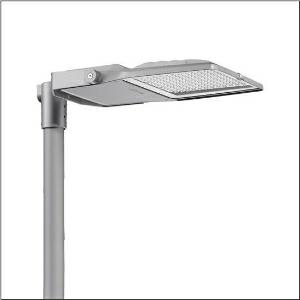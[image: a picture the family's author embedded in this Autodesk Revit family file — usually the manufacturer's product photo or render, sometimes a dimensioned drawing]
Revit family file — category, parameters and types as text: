
# Revit family: floodlight_fl_21_iq_midi___pl33t_5xa7781f4f3a_8e83
name_source: partatom
category: Lighting Fixtures
units: mm (PartAtom-declared; Revit-internal decimal feet)

## family parameters
Cut with Voids When Loaded = No
Host = Face
Light Source = No
Part Type = Normal
Room Calculation Point = No
Round Connector Dimension = Use Diameter
Shared = No

## types (1)
- --- (1 x LED, 36900 lm, 270.2 W, 4000K)
    Apparent Load = 270 VA
    CIE Flux Codes = 26 75 99 100 100
    Color Rendering = 70
    Color Temperature = 4000K
    Default Elevation = 1800 mm
    Description = Floodlight FL 21 iQ midi, floodlight, primary light control with lens, of PMMA, primary optical cover: protective disc, of toughened safety glass, transparent, light distribution: PL33T, light emission: direct distribution, installation type: surface-mounted, LED, High Power LED, rated luminous flux: 36.900lm, luminous efficacy: 137lm/W, light colour: 740, colour temperature: 4000K, control gear: iQ Comfort/DALI, control: optimised constant luminous flux control (CLO 2.0), Desk-Remote (wireless, voltage-free reading and setting of iQ features in the workshop via application-optimized NFC function/RFID function), Light-Fading, Smart-Wire, Night-Set, Lumen-Switch, Temp-Guard, Auto-Match, with terminal, 6-pole, mains connection: 220..240V, AC, 50/60Hz, start of lifetime: 270W, end of service life: 287W, reduction: 118W, luminaire housing, of diecast aluminium, powder-coated, Siteco® metallic grey (DB 702S), corrosivity category C5 mid according to DIN EN ISO 12944, suitable for swimming pools, chlorine-resistant, sealing non-destructively replaceable, please order mast flange separately, mast bracket, of steel, galvanised, powder-coated, Siteco® metallic grey (DB 702S), protection rating (complete): IP66, insulation class (complete): insulation class II (safety insulation), certification: CE, ENEC, VDE, protection symbol: D, impact resistance: IK08, permissible operating ambient temperature: -40..+40°C, permissible operating ambient temperature for outdoor applications: -40..+50°C, standard: DIN EN 12944, LABS conformity tested according to VDMA 24364:2018-05, packaging unit: 1 piece

Light Distribution: PL33T
    Height = 76 mm
    Lamp = 1 x LED
    Lamp Light Flux = 36900 lm
    Lamp Power = 270.2 W
    Lamp count = 1
    Length = 657 mm
    Luminous efficacy = 137 lm/W
    Manufacturer = Siteco
    ModVariant = No
    Model = 5XA7781F4F3A
    Number of Poles = 1
    OnlyDefault = Yes
    Power Factor = 1
    Product Name = Floodlight FL 21 iQ midi | PL33T
    Product group = floodlight | pylon annexe
    ProductGroupID = 6200
    Protection Class = Protection class II
    Protection Degree = IP 66
    RLX_Detail_Level = 1
    RLX_Emergency_Light_Flux = 0 lm
    RLX_Emergency_Type = 0
    RLX_Emergency_Type_DB = No
    RlxData = <blob elided: 153625 chars, md5=2b8e885d>
    Socket = socket
    Standby Power = 0 W
    System Light Flux = 36900 lm
    System Power = 270 W
    Type Comments = factory setting: luminous flux: 100 % | dim-lin: 254 | 620 mA
    Type Image = l_1007123.jpg
    URL = http://relux.com
    VarID = @adj_103488
    Voltage = 0 V
    Weight = 0.00 kg
    Width = 442 mm

## geometry (parser evidence)
native form markers: Blend x4, Sweep x13
no freeform markers — native parametric forms only
